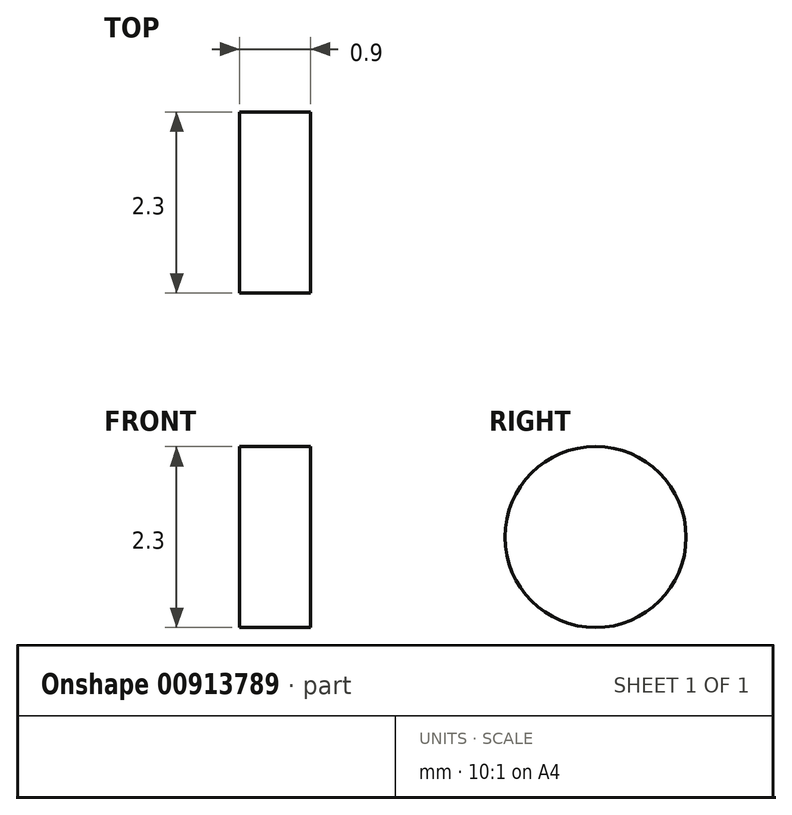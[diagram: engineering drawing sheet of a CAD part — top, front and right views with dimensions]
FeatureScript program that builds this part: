
annotation { "Feature Type Name" : "Feature", "Feature Type Description" : "" }
export const myFeature = defineFeature(function(context is Context, id is Id, definition is map)
    precondition{}
    {
        {
            var Q0;
            Q0=qCreatedBy(makeId("Right.planeOp"),FACE);
            var sketch = newSketch(context, id + "F0", { "sketchPlane" : qUnion([Q0])});
            skCircle(sketch, "E0", {"center": v(0, 0) * mm, "radius": 1.15 * mm});
            skSolve(sketch);
        }
        {
            var Q0;
            Q0 = qSketchRegion(id + "F0", true);
            extrude(context, id + "F1", {"entities" : qUnion([Q0]), "depth" : 0.9 * mm, "offsetDistance" : 25.4 * mm});
        }
    });
